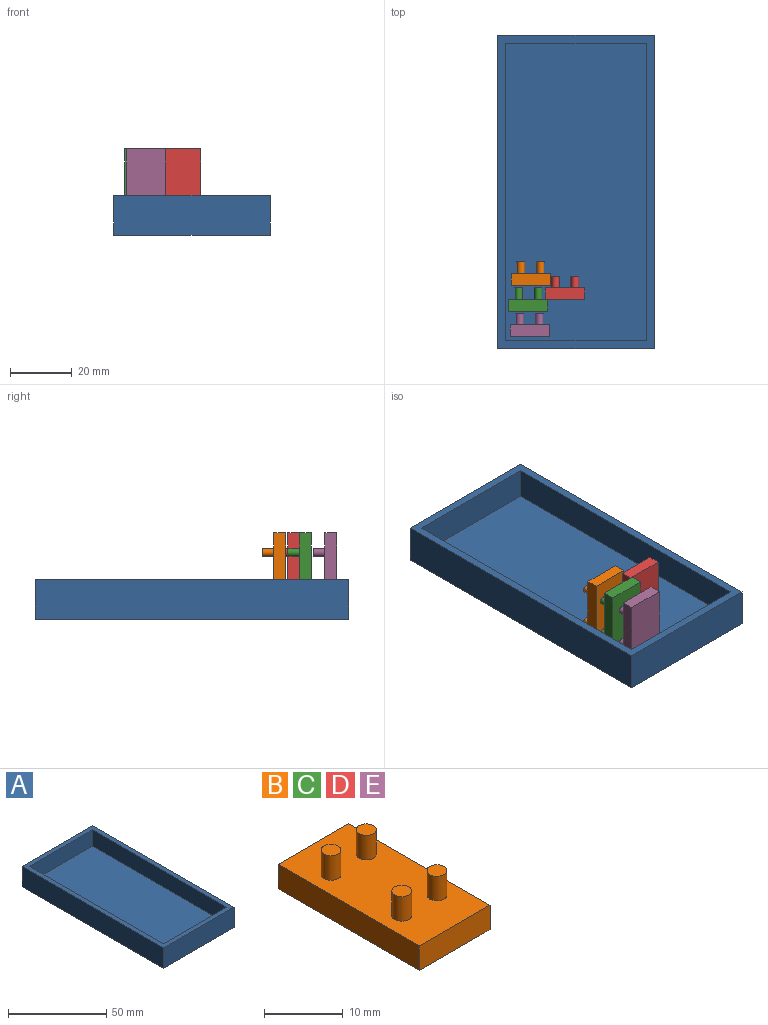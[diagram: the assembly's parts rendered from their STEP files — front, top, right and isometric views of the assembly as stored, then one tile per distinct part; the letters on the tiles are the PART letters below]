
ASSEMBLY  parts=5 mates=4
PART A: 11 faces, bbox 50.8x101.6x12.7 mm
  f0: plane 101.6x50.8mm, normal (0,0,1), area 748.4mm2, adj f1,f2,f3,f4,f6,f7,f8,f9
  f1: plane 50.8x12.7mm, normal (0,-1,0), area 645.2mm2, adj f0,f2,f4,f5
  f2: plane 101.6x12.7mm, normal (1,0,0), area 1290.3mm2, adj f0,f1,f3,f5
  f3: plane 50.8x12.7mm, normal (0,1,0), area 645.2mm2, adj f0,f2,f4,f5
  f4: plane 101.6x12.7mm, normal (-1,0,0), area 1290.3mm2, adj f0,f1,f3,f5
  f5: plane 101.6x50.8mm, normal (0,0,-1), area 5161.3mm2, adj f1,f2,f3,f4
  f6: plane 45.72x10.16mm, normal (0,1,0), area 464.5mm2, adj f0,f7,f9,f10
  f7: plane 96.52x10.16mm, normal (-1,0,0), area 980.6mm2, adj f0,f6,f8,f10
  f8: plane 45.72x10.16mm, normal (0,-1,0), area 464.5mm2, adj f0,f7,f9,f10
  f9: plane 96.52x10.16mm, normal (1,0,0), area 980.6mm2, adj f0,f6,f8,f10
  f10: plane 96.52x45.72mm, normal (0,0,1), area 4412.9mm2, adj f6,f7,f8,f9
PART B: 14 faces, bbox 12.7x25.4x7.6 mm
  f0: plane 12.7x3.81mm, normal (0,-1,0), area 48.4mm2, adj f1,f3,f4,f5
  f1: plane 25.4x3.81mm, normal (1,0,0), area 96.8mm2, adj f0,f2,f4,f5
  f2: plane 12.7x3.81mm, normal (0,1,0), area 48.4mm2, adj f1,f3,f4,f5
  f3: plane 25.4x3.81mm, normal (-1,0,0), area 96.8mm2, adj f0,f2,f4,f5
  f4: plane 25.4x12.7mm, normal (0,0,1), area 302.3mm2, adj f0,f1,f2,f3,f6,f8,f10,f12
  f5: plane 25.4x12.7mm, normal (0,0,-1), area 322.6mm2, adj f0,f1,f2,f3
  f6: cylinder r=1.27mm len=3.81mm, axis (0,0,-1), area 30.4mm2, adj f4,f7
  f7: plane 2.54x2.54mm, normal (0,0,1), area 5.1mm2, adj f6
  f8: cylinder r=1.27mm len=3.81mm, axis (0,0,-1), area 30.4mm2, adj f4,f9
  f9: plane 2.54x2.54mm, normal (0,0,1), area 5.1mm2, adj f8
  f10: cylinder r=1.27mm len=3.81mm, axis (0,0,-1), area 30.4mm2, adj f4,f11
  f11: plane 2.54x2.54mm, normal (0,0,1), area 5.1mm2, adj f10
  f12: cylinder r=1.27mm len=3.81mm, axis (0,0,-1), area 30.4mm2, adj f4,f13
  f13: plane 2.54x2.54mm, normal (0,0,1), area 5.1mm2, adj f12
PART C: same geometry as B
PART D: same geometry as B
PART E: same geometry as B
PLACE A t=(-23.74,-12.79,9.97)mm
PLACE B rot(axis=(-1,0,0),90deg) t=(-38.47,-43.14,25.21)mm
PLACE C rot(axis=(-1,0,0),90deg) t=(-39.23,-51.52,25.21)mm
PLACE D rot(axis=(-1,0,0),90deg) t=(-27.29,-47.71,25.21)mm
PLACE E rot(axis=(-1,0,0),90deg) t=(-38.8,-59.73,25.21)mm
MATE planar D.f2 <-> A.f10  axis (0,0,-1) through (-27.29,-45.81,12.51)mm
MATE planar E.f2 <-> A.f10  axis (0,0,-1) through (-38.8,-57.82,12.51)mm
MATE planar C.f2 <-> A.f10  axis (0,0,-1) through (-39.23,-49.62,12.51)mm
MATE planar B.f2 <-> A.f10  axis (0,0,-1) through (-38.47,-41.24,12.51)mm
